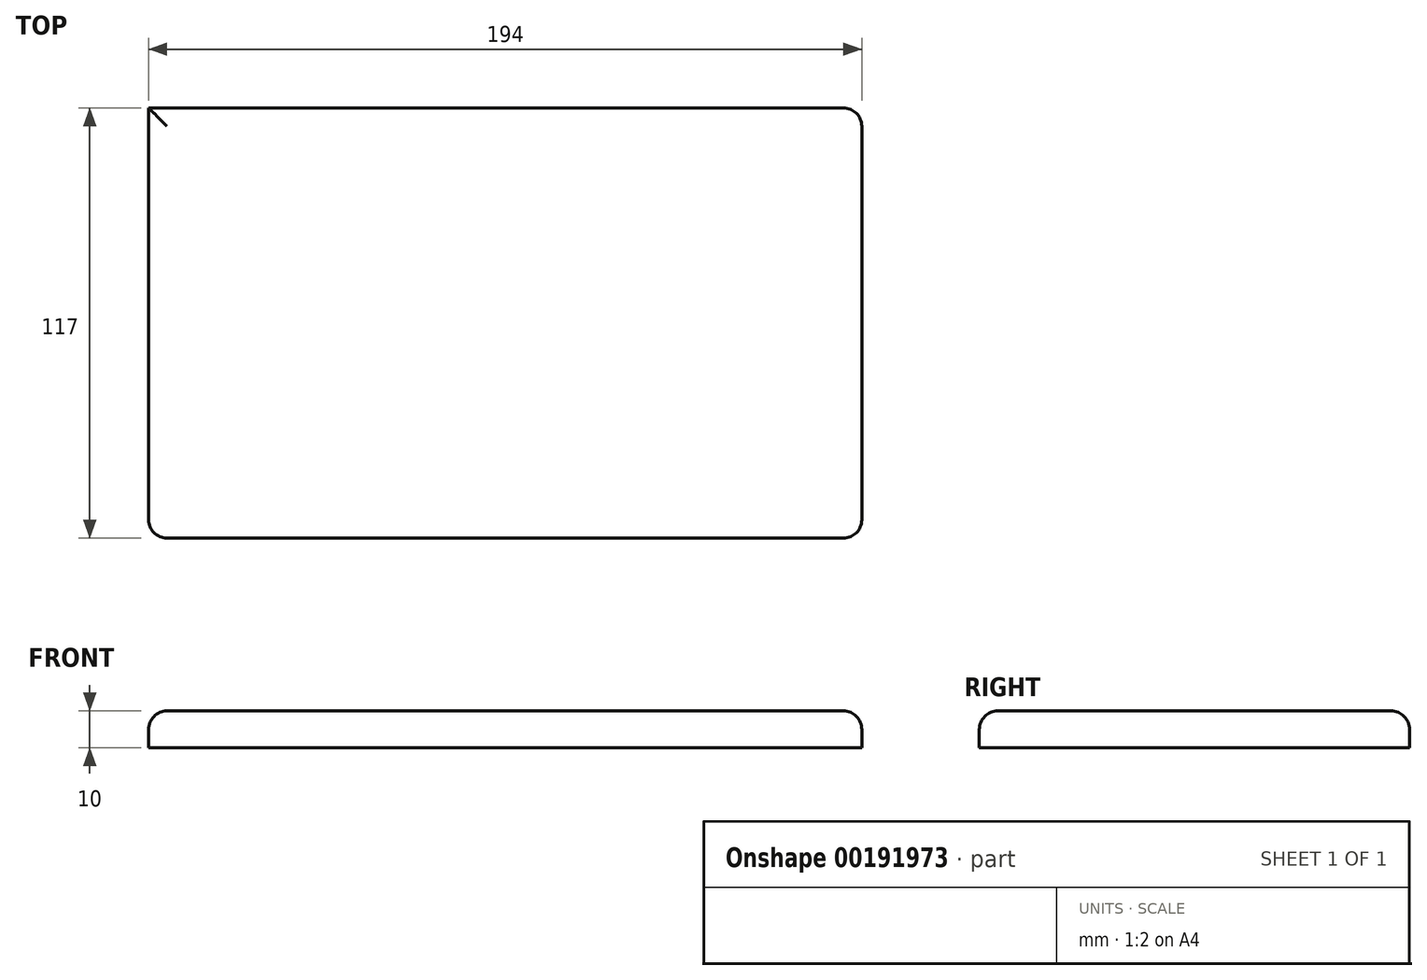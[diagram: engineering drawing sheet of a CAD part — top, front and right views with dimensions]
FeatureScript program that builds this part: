
annotation { "Feature Type Name" : "Feature", "Feature Type Description" : "" }
export const myFeature = defineFeature(function(context is Context, id is Id, definition is map)
    precondition{}
    {
        {
            var Q0;
            Q0=qCreatedBy(makeId("Top.planeOp"),FACE);
            var sketch = newSketch(context, id + "F0", { "sketchPlane" : qUnion([Q0])});
            skLineSegment(sketch, "E0.bottom", {"start": v(-97, 58.5) * mm, "end": v(97, 58.5) * mm});
            skLineSegment(sketch, "E0.top", {"start": v(-97, -58.5) * mm, "end": v(97, -58.5) * mm});
            skLineSegment(sketch, "E0.left", {"start": v(-97, 58.5) * mm, "end": v(-97, -58.5) * mm});
            skLineSegment(sketch, "E0.right", {"start": v(97, 58.5) * mm, "end": v(97, -58.5) * mm});
            skPoint(sketch, "E0.middle", {"position": v(0, 0) * mm});
            skSolve(sketch);
        }
        {
            var Q0;
            Q0=makeQuery(id+"F0.imprint","IMPRINT",FACE,{"disambiguationData":[TD([[makeQuery(id+"F0.imprint","IMPRINT",EDGE,{"derivedFrom":sQuery(id+"F0.wireOp",EDGE,"E0.bottom")}),-1.0]])]});
            extrude(context, id + "F1", {"entities" : qUnion([Q0]), "depth" : 10 * mm});
        }
        {
            var Q0;
            Q0=makeQuery(id+"F1.opExtrude","CAP_EDGE",EDGE,{"disambiguationData":[OSD([sQuery(id+"F0.wireOp",EDGE,"E0.top")])],"isStart":false});
            fillet(context, id + "F2", {"entities" : qUnion([Q0]), "radius" : 5 * mm, "tangentPropagation" : true, "allowEdgeOverflow" : false});
        }
        {
            var Q0;
            {var subQ0=sQuery(id+"F0.wireOp",EDGE,"E0.top");Q0=makeQuery(id+"F2.opFillet","BLEND_EDGE",EDGE,{"blendedFrom":[makeQuery(id+"F1.opExtrude","CAP_EDGE",EDGE,{"disambiguationData":[OSD([subQ0])],"isStart":false}),makeQuery(id+"F1.opExtrude","SWEPT_FACE",FACE,{"disambiguationData":[OSD([subQ0])]})],"blendedInto":[makeQuery(id+"F1.opExtrude","SWEPT_FACE",FACE,{"disambiguationData":[OSD([subQ0])]})]});}
            var Q1;
            Q1=makeQuery(id+"F2.opFillet","BLEND_EDGE",EDGE,{"blendedFrom":[makeQuery(id+"F1.opExtrude","CAP_EDGE",EDGE,{"disambiguationData":[OSD([sQuery(id+"F0.wireOp",EDGE,"E0.top")])],"isStart":false}),makeQuery(id+"F1.opExtrude","SWEPT_FACE",FACE,{"disambiguationData":[OSD([sQuery(id+"F0.wireOp",EDGE,"E0.right")])]})],"blendedInto":[makeQuery(id+"F1.opExtrude","SWEPT_FACE",FACE,{"disambiguationData":[OSD([sQuery(id+"F0.wireOp",EDGE,"E0.right")])]})]});
            fillet(context, id + "F3", {"entities" : qUnion([Q0, Q1]), "radius" : 5 * mm, "tangentPropagation" : true, "allowEdgeOverflow" : false});
        }
        {
            var Q0;
            {var subQ0=sQuery(id+"F0.wireOp",EDGE,"E0.right");Q0=makeQuery(id+"F3.opFillet","BLEND_EDGE",EDGE,{"blendedFrom":[makeQuery(id+"F1.opExtrude","CAP_EDGE",EDGE,{"disambiguationData":[OSD([subQ0])],"isStart":false}),makeQuery(id+"F1.opExtrude","SWEPT_FACE",FACE,{"disambiguationData":[OSD([subQ0])]})],"blendedInto":[makeQuery(id+"F1.opExtrude","SWEPT_FACE",FACE,{"disambiguationData":[OSD([subQ0])]})]});}
            var Q1;
            Q1=makeQuery(id+"F3.opFillet","BLEND_EDGE",EDGE,{"blendedFrom":[makeQuery(id+"F1.opExtrude","CAP_EDGE",EDGE,{"disambiguationData":[OSD([sQuery(id+"F0.wireOp",EDGE,"E0.right")])],"isStart":false}),makeQuery(id+"F1.opExtrude","SWEPT_FACE",FACE,{"disambiguationData":[OSD([sQuery(id+"F0.wireOp",EDGE,"E0.bottom")])]})],"blendedInto":[makeQuery(id+"F1.opExtrude","SWEPT_FACE",FACE,{"disambiguationData":[OSD([sQuery(id+"F0.wireOp",EDGE,"E0.bottom")])]})]});
            var Q2;
            Q2=makeQuery(id+"F2.opFillet","BLEND_EDGE",EDGE,{"blendedFrom":[makeQuery(id+"F1.opExtrude","CAP_EDGE",EDGE,{"disambiguationData":[OSD([sQuery(id+"F0.wireOp",EDGE,"E0.top")])],"isStart":false}),makeQuery(id+"F1.opExtrude","SWEPT_FACE",FACE,{"disambiguationData":[OSD([sQuery(id+"F0.wireOp",EDGE,"E0.left")])]})],"blendedInto":[makeQuery(id+"F1.opExtrude","SWEPT_FACE",FACE,{"disambiguationData":[OSD([sQuery(id+"F0.wireOp",EDGE,"E0.left")])]})]});
            fillet(context, id + "F4", {"entities" : qUnion([Q0, Q1, Q2]), "radius" : 5 * mm, "tangentPropagation" : true, "allowEdgeOverflow" : false});
        }
    });
